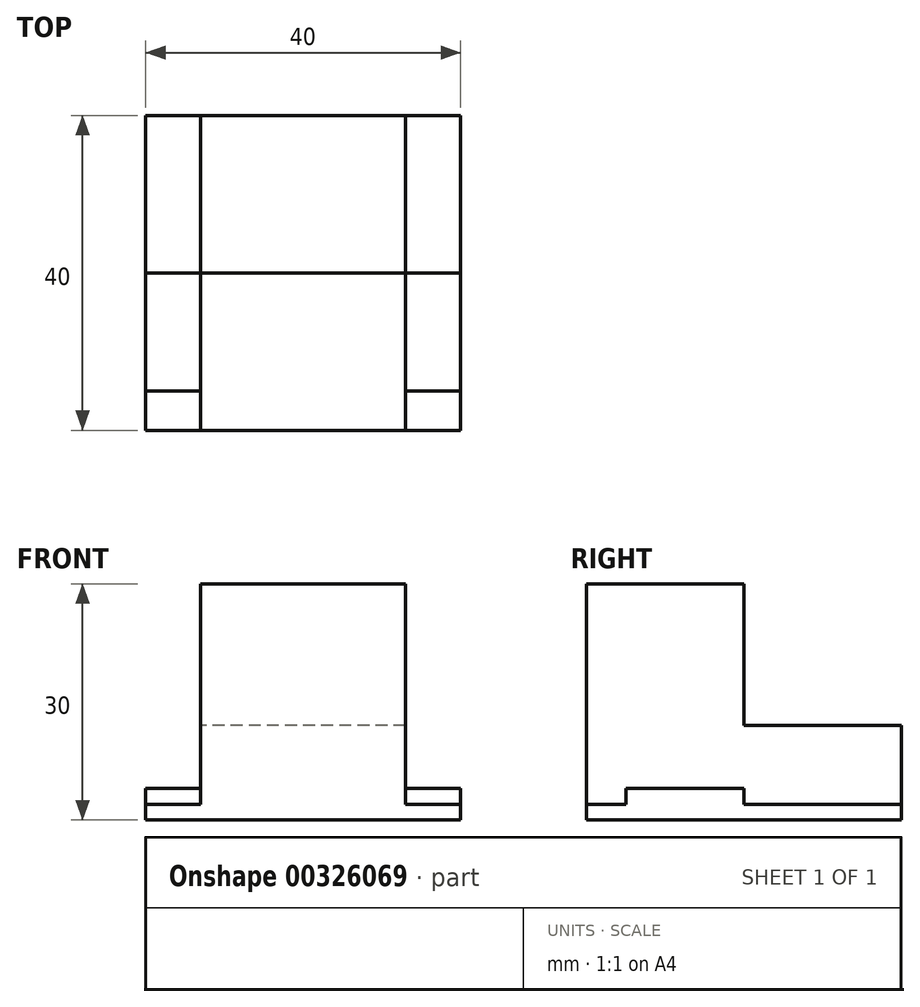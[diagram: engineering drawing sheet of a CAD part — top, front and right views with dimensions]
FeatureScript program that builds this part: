
annotation { "Feature Type Name" : "Feature", "Feature Type Description" : "" }
export const myFeature = defineFeature(function(context is Context, id is Id, definition is map)
    precondition{}
    {
        {
            var Q0;
            Q0=qCreatedBy(makeId("Top.planeOp"),FACE);
            var sketch = newSketch(context, id + "F0", { "sketchPlane" : qUnion([Q0])});
            skLineSegment(sketch, "E0.bottom", {"start": v(20, 20) * mm, "end": v(-20, 20) * mm});
            skLineSegment(sketch, "E0.top", {"start": v(20, -20) * mm, "end": v(-20, -20) * mm});
            skLineSegment(sketch, "E0.left", {"start": v(20, 20) * mm, "end": v(20, -20) * mm});
            skLineSegment(sketch, "E0.right", {"start": v(-20, 20) * mm, "end": v(-20, -20) * mm});
            skPoint(sketch, "E0.middle", {"position": v(0, 0) * mm});
            skLineSegment(sketch, "E1.bottom", {"start": v(13, 0) * mm, "end": v(-13, 0) * mm});
            skLineSegment(sketch, "E1.top", {"start": v(13, -20) * mm, "end": v(-13, -20) * mm});
            skLineSegment(sketch, "E1.left", {"start": v(13, 0) * mm, "end": v(13, -20) * mm});
            skLineSegment(sketch, "E1.right", {"start": v(-13, 0) * mm, "end": v(-13, -20) * mm});
            skPoint(sketch, "E1.middle", {"position": v(0, -10) * mm});
            skSolve(sketch);
        }
        {
            var Q0;
            Q0=makeQuery(id+"F0.imprint","IMPRINT",FACE,{"disambiguationData":[TD([[makeQuery(id+"F0.imprint","IMPRINT",EDGE,{"derivedFrom":sQuery(id+"F0.wireOp",EDGE,"E0.bottom")}),1.0]])]});
            extrude(context, id + "F1", {"entities" : qUnion([Q0]), "depth" : 2 * mm});
        }
        {
            var Q0;
            Q0=makeQuery(id+"F0.imprint","IMPRINT",FACE,{"disambiguationData":[TD([[makeQuery(id+"F0.imprint","IMPRINT",EDGE,{"derivedFrom":sQuery(id+"F0.wireOp",EDGE,"E1.bottom")}),1.0]])]});
            extrude(context, id + "F2", {"entities" : qUnion([Q0]), "depth" : 30 * mm});
        }
        {
            var Q0;
            Q0=makeQuery(id+"F1.opExtrude","CAP_FACE",FACE,{"disambiguationData":[OSD([sQuery(id+"F0.wireOp",EDGE,"E0.bottom"),sQuery(id+"F0.wireOp",EDGE,"E0.top"),sQuery(id+"F0.wireOp",EDGE,"E0.left"),sQuery(id+"F0.wireOp",EDGE,"E0.right"),sQuery(id+"F0.wireOp",EDGE,"E1.bottom"),sQuery(id+"F0.wireOp",EDGE,"E1.left"),sQuery(id+"F0.wireOp",EDGE,"E1.right")])],"isStart":false});
            var sketch = newSketch(context, id + "F3", { "sketchPlane" : qUnion([Q0])});
            skLineSegment(sketch, "E2.bottom", {"start": v(-13, 20) * mm, "end": v(13, 20) * mm});
            skLineSegment(sketch, "E2.top", {"start": v(-13, 0) * mm, "end": v(13, 0) * mm});
            skLineSegment(sketch, "E2.left", {"start": v(-13, 20) * mm, "end": v(-13, 0) * mm});
            skLineSegment(sketch, "E2.right", {"start": v(13, 20) * mm, "end": v(13, 0) * mm});
            skSolve(sketch);
        }
        {
            var Q0;
            Q0=makeQuery(id+"F3.imprint","IMPRINT",FACE,{"disambiguationData":[TD([[makeQuery(id+"F3.imprint","IMPRINT",EDGE,{"derivedFrom":sQuery(id+"F3.wireOp",EDGE,"E2.bottom")}),1.0]])]});
            extrude(context, id + "F4", {"entities" : qUnion([Q0]), "operationType" : NewBodyOperationType.ADD, "depth" : 10 * mm});
        }
        {
            var Q0;
            {var subQ0=sQuery(id+"F0.wireOp",EDGE,"E0.right");var subQ1=sQuery(id+"F0.wireOp",EDGE,"E0.top");var subQ2=sQuery(id+"F0.wireOp",EDGE,"E1.right");var subQ4=sQuery(id+"F0.wireOp",EDGE,"E0.left");var subQ5=sQuery(id+"F0.wireOp",EDGE,"E1.left");var subQ6=sQuery(id+"F0.wireOp",EDGE,"E0.bottom");Q0=makeQuery(id+"F4.boolean.opBoolean","SPLIT",FACE,{"disambiguationData":[TD([makeQuery(id+"F1.opExtrude","SWEPT_FACE",FACE,{"disambiguationData":[OSD([subQ4])]})])],"derivedFrom":makeQuery(id+"F1.opExtrude","CAP_FACE",FACE,{"disambiguationData":[OSD([subQ6,subQ1,subQ4,subQ0,sQuery(id+"F0.wireOp",EDGE,"E1.bottom"),subQ5,subQ2])],"isStart":false})});}
            var sketch = newSketch(context, id + "F5", { "sketchPlane" : qUnion([Q0])});
            skLineSegment(sketch, "E3.bottom", {"start": v(20, -15) * mm, "end": v(13, -15) * mm});
            skLineSegment(sketch, "E3.top", {"start": v(20, 0) * mm, "end": v(13, 0) * mm});
            skLineSegment(sketch, "E3.left", {"start": v(20, -15) * mm, "end": v(20, 0) * mm});
            skLineSegment(sketch, "E3.right", {"start": v(13, -15) * mm, "end": v(13, 0) * mm});
            skLineSegment(sketch, "E4.bottom", {"start": v(-20, -15) * mm, "end": v(-13, -15) * mm});
            skLineSegment(sketch, "E4.top", {"start": v(-20, 0) * mm, "end": v(-13, 0) * mm});
            skLineSegment(sketch, "E4.left", {"start": v(-20, -15) * mm, "end": v(-20, 0) * mm});
            skLineSegment(sketch, "E4.right", {"start": v(-13, -15) * mm, "end": v(-13, 0) * mm});
            skSolve(sketch);
        }
        {
            var Q0;
            Q0=makeQuery(id+"F5.imprint","IMPRINT",FACE,{"disambiguationData":[TD([[makeQuery(id+"F5.imprint","IMPRINT",EDGE,{"derivedFrom":sQuery(id+"F5.wireOp",EDGE,"E3.bottom")}),-1.0]])]});
            var Q1;
            Q1=makeQuery(id+"F5.imprint","IMPRINT",FACE,{"disambiguationData":[TD([[makeQuery(id+"F5.imprint","IMPRINT",EDGE,{"derivedFrom":sQuery(id+"F5.wireOp",EDGE,"E4.bottom")}),1.0]])]});
            extrude(context, id + "F6", {"entities" : qUnion([Q0, Q1]), "operationType" : NewBodyOperationType.ADD, "depth" : 2 * mm});
        }
    });
